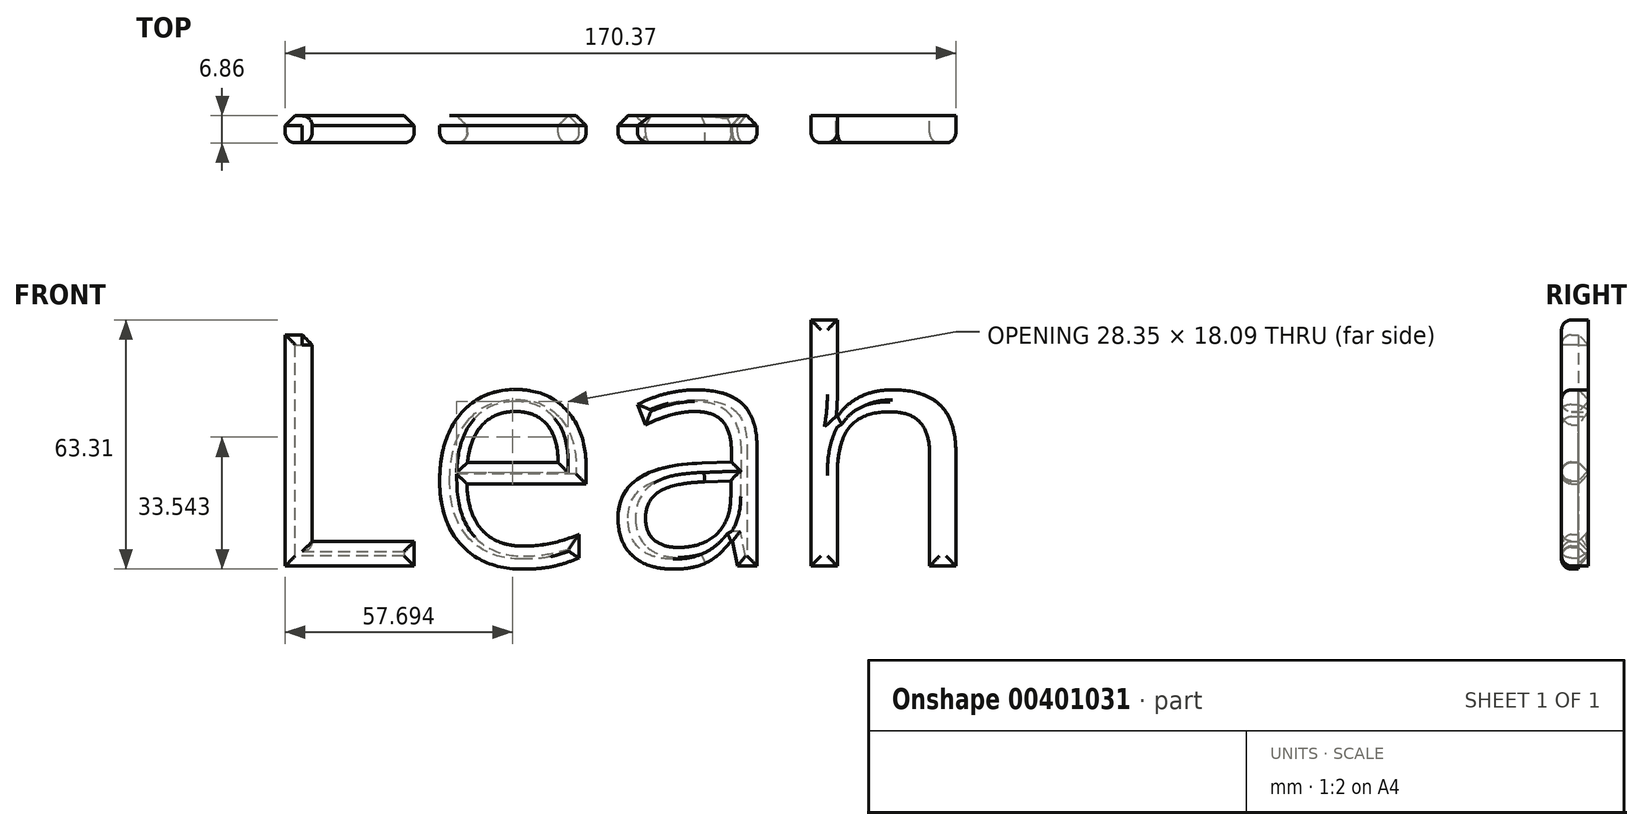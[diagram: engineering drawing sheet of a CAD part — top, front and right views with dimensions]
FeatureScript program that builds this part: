
annotation { "Feature Type Name" : "Feature", "Feature Type Description" : "" }
export const myFeature = defineFeature(function(context is Context, id is Id, definition is map)
    precondition{}
    {
        {
            var Q0;
            Q0=qCreatedBy(makeId("Front.planeOp"),FACE);
            var sketch = newSketch(context, id + "F0", { "sketchPlane" : qUnion([Q0])});
            skText(sketch, "E0", { "text": "Leah", "fontName": "OpenSans-Regular.ttf"});
            const initialGuessF0  = {"E0": [-0.10363, -0.03203, 1, 0, 0.05922]};
            skSetInitialGuess(sketch, initialGuessF0);
            skSolve(sketch);
        }
        {
            var Q0;
            Q0 = qSketchRegion(id + "F0", true);
            extrude(context, id + "F1", {"entities" : qUnion([Q0]), "depth" : 6.86 * mm});
        }
        {
            var Q0;
            Q0=makeQuery(id+"F1.opExtrude","CAP_FACE",FACE,{"disambiguationData":[OSD([sQuery(id+"F0.wireOp",EDGE,"E0.sketch_text.stroke-0"),sQuery(id+"F0.wireOp",EDGE,"E0.sketch_text.stroke-1"),sQuery(id+"F0.wireOp",EDGE,"E0.sketch_text.stroke-2"),sQuery(id+"F0.wireOp",EDGE,"E0.sketch_text.stroke-3"),sQuery(id+"F0.wireOp",EDGE,"E0.sketch_text.stroke-4"),sQuery(id+"F0.wireOp",EDGE,"E0.sketch_text.stroke-5")])],"isStart":false});
            var Q1;
            Q1=makeQuery(id+"F1.opExtrude","CAP_EDGE",EDGE,{"disambiguationData":[OSD([sQuery(id+"F0.wireOp",EDGE,"E0.sketch_text.stroke-3")])],"isStart":false});
            var Q2;
            Q2=makeQuery(id+"F1.opExtrude","CAP_EDGE",EDGE,{"disambiguationData":[OSD([sQuery(id+"F0.wireOp",EDGE,"E0.sketch_text.stroke-2")])],"isStart":true});
            var Q3;
            Q3=makeQuery(id+"F1.opExtrude","CAP_EDGE",EDGE,{"disambiguationData":[OSD([sQuery(id+"F0.wireOp",EDGE,"E0.sketch_text.stroke-22")])],"isStart":false});
            fillet(context, id + "F2", {"entities" : qUnion([Q0, Q1, Q2, Q3]), "radius" : 2.54 * mm, "tangentPropagation" : true, "allowEdgeOverflow" : false});
        }
        {
            var Q0;
            Q0=makeQuery(id+"F1.opExtrude","CAP_FACE",FACE,{"disambiguationData":[OSD([sQuery(id+"F0.wireOp",EDGE,"E0.sketch_text.stroke-6"),sQuery(id+"F0.wireOp",EDGE,"E0.sketch_text.stroke-7"),sQuery(id+"F0.wireOp",EDGE,"E0.sketch_text.stroke-8"),sQuery(id+"F0.wireOp",EDGE,"E0.sketch_text.stroke-9"),sQuery(id+"F0.wireOp",EDGE,"E0.sketch_text.stroke-10"),sQuery(id+"F0.wireOp",EDGE,"E0.sketch_text.stroke-11"),sQuery(id+"F0.wireOp",EDGE,"E0.sketch_text.stroke-12"),sQuery(id+"F0.wireOp",EDGE,"E0.sketch_text.stroke-13"),sQuery(id+"F0.wireOp",EDGE,"E0.sketch_text.stroke-14"),sQuery(id+"F0.wireOp",EDGE,"E0.sketch_text.stroke-15"),sQuery(id+"F0.wireOp",EDGE,"E0.sketch_text.stroke-16"),sQuery(id+"F0.wireOp",EDGE,"E0.sketch_text.stroke-17"),sQuery(id+"F0.wireOp",EDGE,"E0.sketch_text.stroke-18"),sQuery(id+"F0.wireOp",EDGE,"E0.sketch_text.stroke-19"),sQuery(id+"F0.wireOp",EDGE,"E0.sketch_text.stroke-20"),sQuery(id+"F0.wireOp",EDGE,"E0.sketch_text.stroke-21"),sQuery(id+"F0.wireOp",EDGE,"E0.sketch_text.stroke-22"),sQuery(id+"F0.wireOp",EDGE,"E0.sketch_text.stroke-23"),sQuery(id+"F0.wireOp",EDGE,"E0.sketch_text.stroke-24")])],"isStart":false});
            var Q1;
            Q1=makeQuery(id+"F1.opExtrude","CAP_FACE",FACE,{"disambiguationData":[OSD([sQuery(id+"F0.wireOp",EDGE,"E0.sketch_text.stroke-25"),sQuery(id+"F0.wireOp",EDGE,"E0.sketch_text.stroke-26"),sQuery(id+"F0.wireOp",EDGE,"E0.sketch_text.stroke-27"),sQuery(id+"F0.wireOp",EDGE,"E0.sketch_text.stroke-28"),sQuery(id+"F0.wireOp",EDGE,"E0.sketch_text.stroke-29"),sQuery(id+"F0.wireOp",EDGE,"E0.sketch_text.stroke-30"),sQuery(id+"F0.wireOp",EDGE,"E0.sketch_text.stroke-31"),sQuery(id+"F0.wireOp",EDGE,"E0.sketch_text.stroke-32"),sQuery(id+"F0.wireOp",EDGE,"E0.sketch_text.stroke-33"),sQuery(id+"F0.wireOp",EDGE,"E0.sketch_text.stroke-34"),sQuery(id+"F0.wireOp",EDGE,"E0.sketch_text.stroke-35"),sQuery(id+"F0.wireOp",EDGE,"E0.sketch_text.stroke-36"),sQuery(id+"F0.wireOp",EDGE,"E0.sketch_text.stroke-37"),sQuery(id+"F0.wireOp",EDGE,"E0.sketch_text.stroke-38"),sQuery(id+"F0.wireOp",EDGE,"E0.sketch_text.stroke-39"),sQuery(id+"F0.wireOp",EDGE,"E0.sketch_text.stroke-40"),sQuery(id+"F0.wireOp",EDGE,"E0.sketch_text.stroke-41"),sQuery(id+"F0.wireOp",EDGE,"E0.sketch_text.stroke-42"),sQuery(id+"F0.wireOp",EDGE,"E0.sketch_text.stroke-43"),sQuery(id+"F0.wireOp",EDGE,"E0.sketch_text.stroke-44"),sQuery(id+"F0.wireOp",EDGE,"E0.sketch_text.stroke-45"),sQuery(id+"F0.wireOp",EDGE,"E0.sketch_text.stroke-46"),sQuery(id+"F0.wireOp",EDGE,"E0.sketch_text.stroke-47"),sQuery(id+"F0.wireOp",EDGE,"E0.sketch_text.stroke-48"),sQuery(id+"F0.wireOp",EDGE,"E0.sketch_text.stroke-49"),sQuery(id+"F0.wireOp",EDGE,"E0.sketch_text.stroke-50"),sQuery(id+"F0.wireOp",EDGE,"E0.sketch_text.stroke-51")])],"isStart":false});
            var Q2;
            Q2=makeQuery(id+"F1.opExtrude","CAP_FACE",FACE,{"disambiguationData":[OSD([sQuery(id+"F0.wireOp",EDGE,"E0.sketch_text.stroke-52"),sQuery(id+"F0.wireOp",EDGE,"E0.sketch_text.stroke-53"),sQuery(id+"F0.wireOp",EDGE,"E0.sketch_text.stroke-54"),sQuery(id+"F0.wireOp",EDGE,"E0.sketch_text.stroke-55"),sQuery(id+"F0.wireOp",EDGE,"E0.sketch_text.stroke-56"),sQuery(id+"F0.wireOp",EDGE,"E0.sketch_text.stroke-57"),sQuery(id+"F0.wireOp",EDGE,"E0.sketch_text.stroke-58"),sQuery(id+"F0.wireOp",EDGE,"E0.sketch_text.stroke-59"),sQuery(id+"F0.wireOp",EDGE,"E0.sketch_text.stroke-60"),sQuery(id+"F0.wireOp",EDGE,"E0.sketch_text.stroke-61"),sQuery(id+"F0.wireOp",EDGE,"E0.sketch_text.stroke-62"),sQuery(id+"F0.wireOp",EDGE,"E0.sketch_text.stroke-63"),sQuery(id+"F0.wireOp",EDGE,"E0.sketch_text.stroke-64"),sQuery(id+"F0.wireOp",EDGE,"E0.sketch_text.stroke-65"),sQuery(id+"F0.wireOp",EDGE,"E0.sketch_text.stroke-66"),sQuery(id+"F0.wireOp",EDGE,"E0.sketch_text.stroke-67"),sQuery(id+"F0.wireOp",EDGE,"E0.sketch_text.stroke-68"),sQuery(id+"F0.wireOp",EDGE,"E0.sketch_text.stroke-69")])],"isStart":false});
            fillet(context, id + "F3", {"entities" : qUnion([Q0, Q1, Q2]), "radius" : 2.54 * mm, "tangentPropagation" : true, "allowEdgeOverflow" : false});
        }
        {
            var Q0;
            Q0=makeQuery(id+"F1.opExtrude","CAP_FACE",FACE,{"disambiguationData":[OSD([sQuery(id+"F0.wireOp",EDGE,"E0.sketch_text.stroke-0"),sQuery(id+"F0.wireOp",EDGE,"E0.sketch_text.stroke-1"),sQuery(id+"F0.wireOp",EDGE,"E0.sketch_text.stroke-2"),sQuery(id+"F0.wireOp",EDGE,"E0.sketch_text.stroke-3"),sQuery(id+"F0.wireOp",EDGE,"E0.sketch_text.stroke-4"),sQuery(id+"F0.wireOp",EDGE,"E0.sketch_text.stroke-5")])],"isStart":true});
            chamfer(context, id + "F4", {"entities" : qUnion([Q0]), "width" : 2.54 * mm, "tangentPropagation" : true});
        }
        {
            var Q0;
            Q0=makeQuery(id+"F1.opExtrude","CAP_FACE",FACE,{"disambiguationData":[OSD([sQuery(id+"F0.wireOp",EDGE,"E0.sketch_text.stroke-6"),sQuery(id+"F0.wireOp",EDGE,"E0.sketch_text.stroke-7"),sQuery(id+"F0.wireOp",EDGE,"E0.sketch_text.stroke-8"),sQuery(id+"F0.wireOp",EDGE,"E0.sketch_text.stroke-9"),sQuery(id+"F0.wireOp",EDGE,"E0.sketch_text.stroke-10"),sQuery(id+"F0.wireOp",EDGE,"E0.sketch_text.stroke-11"),sQuery(id+"F0.wireOp",EDGE,"E0.sketch_text.stroke-12"),sQuery(id+"F0.wireOp",EDGE,"E0.sketch_text.stroke-13"),sQuery(id+"F0.wireOp",EDGE,"E0.sketch_text.stroke-14"),sQuery(id+"F0.wireOp",EDGE,"E0.sketch_text.stroke-15"),sQuery(id+"F0.wireOp",EDGE,"E0.sketch_text.stroke-16"),sQuery(id+"F0.wireOp",EDGE,"E0.sketch_text.stroke-17"),sQuery(id+"F0.wireOp",EDGE,"E0.sketch_text.stroke-18"),sQuery(id+"F0.wireOp",EDGE,"E0.sketch_text.stroke-19"),sQuery(id+"F0.wireOp",EDGE,"E0.sketch_text.stroke-20"),sQuery(id+"F0.wireOp",EDGE,"E0.sketch_text.stroke-21"),sQuery(id+"F0.wireOp",EDGE,"E0.sketch_text.stroke-22"),sQuery(id+"F0.wireOp",EDGE,"E0.sketch_text.stroke-23"),sQuery(id+"F0.wireOp",EDGE,"E0.sketch_text.stroke-24")])],"isStart":true});
            var Q1;
            Q1=makeQuery(id+"F1.opExtrude","CAP_FACE",FACE,{"disambiguationData":[OSD([sQuery(id+"F0.wireOp",EDGE,"E0.sketch_text.stroke-25"),sQuery(id+"F0.wireOp",EDGE,"E0.sketch_text.stroke-26"),sQuery(id+"F0.wireOp",EDGE,"E0.sketch_text.stroke-27"),sQuery(id+"F0.wireOp",EDGE,"E0.sketch_text.stroke-28"),sQuery(id+"F0.wireOp",EDGE,"E0.sketch_text.stroke-29"),sQuery(id+"F0.wireOp",EDGE,"E0.sketch_text.stroke-30"),sQuery(id+"F0.wireOp",EDGE,"E0.sketch_text.stroke-31"),sQuery(id+"F0.wireOp",EDGE,"E0.sketch_text.stroke-32"),sQuery(id+"F0.wireOp",EDGE,"E0.sketch_text.stroke-33"),sQuery(id+"F0.wireOp",EDGE,"E0.sketch_text.stroke-34"),sQuery(id+"F0.wireOp",EDGE,"E0.sketch_text.stroke-35"),sQuery(id+"F0.wireOp",EDGE,"E0.sketch_text.stroke-36"),sQuery(id+"F0.wireOp",EDGE,"E0.sketch_text.stroke-37"),sQuery(id+"F0.wireOp",EDGE,"E0.sketch_text.stroke-38"),sQuery(id+"F0.wireOp",EDGE,"E0.sketch_text.stroke-39"),sQuery(id+"F0.wireOp",EDGE,"E0.sketch_text.stroke-40"),sQuery(id+"F0.wireOp",EDGE,"E0.sketch_text.stroke-41"),sQuery(id+"F0.wireOp",EDGE,"E0.sketch_text.stroke-42"),sQuery(id+"F0.wireOp",EDGE,"E0.sketch_text.stroke-43"),sQuery(id+"F0.wireOp",EDGE,"E0.sketch_text.stroke-44"),sQuery(id+"F0.wireOp",EDGE,"E0.sketch_text.stroke-45"),sQuery(id+"F0.wireOp",EDGE,"E0.sketch_text.stroke-46"),sQuery(id+"F0.wireOp",EDGE,"E0.sketch_text.stroke-47"),sQuery(id+"F0.wireOp",EDGE,"E0.sketch_text.stroke-48"),sQuery(id+"F0.wireOp",EDGE,"E0.sketch_text.stroke-49"),sQuery(id+"F0.wireOp",EDGE,"E0.sketch_text.stroke-50"),sQuery(id+"F0.wireOp",EDGE,"E0.sketch_text.stroke-51")])],"isStart":true});
            var Q2;
            Q2=makeQuery(id+"F1.opExtrude","CAP_FACE",FACE,{"disambiguationData":[OSD([sQuery(id+"F0.wireOp",EDGE,"E0.sketch_text.stroke-52"),sQuery(id+"F0.wireOp",EDGE,"E0.sketch_text.stroke-53"),sQuery(id+"F0.wireOp",EDGE,"E0.sketch_text.stroke-54"),sQuery(id+"F0.wireOp",EDGE,"E0.sketch_text.stroke-55"),sQuery(id+"F0.wireOp",EDGE,"E0.sketch_text.stroke-56"),sQuery(id+"F0.wireOp",EDGE,"E0.sketch_text.stroke-57"),sQuery(id+"F0.wireOp",EDGE,"E0.sketch_text.stroke-58"),sQuery(id+"F0.wireOp",EDGE,"E0.sketch_text.stroke-59"),sQuery(id+"F0.wireOp",EDGE,"E0.sketch_text.stroke-60"),sQuery(id+"F0.wireOp",EDGE,"E0.sketch_text.stroke-61"),sQuery(id+"F0.wireOp",EDGE,"E0.sketch_text.stroke-62"),sQuery(id+"F0.wireOp",EDGE,"E0.sketch_text.stroke-63"),sQuery(id+"F0.wireOp",EDGE,"E0.sketch_text.stroke-64"),sQuery(id+"F0.wireOp",EDGE,"E0.sketch_text.stroke-65"),sQuery(id+"F0.wireOp",EDGE,"E0.sketch_text.stroke-66"),sQuery(id+"F0.wireOp",EDGE,"E0.sketch_text.stroke-67"),sQuery(id+"F0.wireOp",EDGE,"E0.sketch_text.stroke-68"),sQuery(id+"F0.wireOp",EDGE,"E0.sketch_text.stroke-69")])],"isStart":true});
            chamfer(context, id + "F5", {"entities" : qUnion([Q0, Q1, Q2]), "width" : 2.54 * mm, "tangentPropagation" : true});
        }
    });
